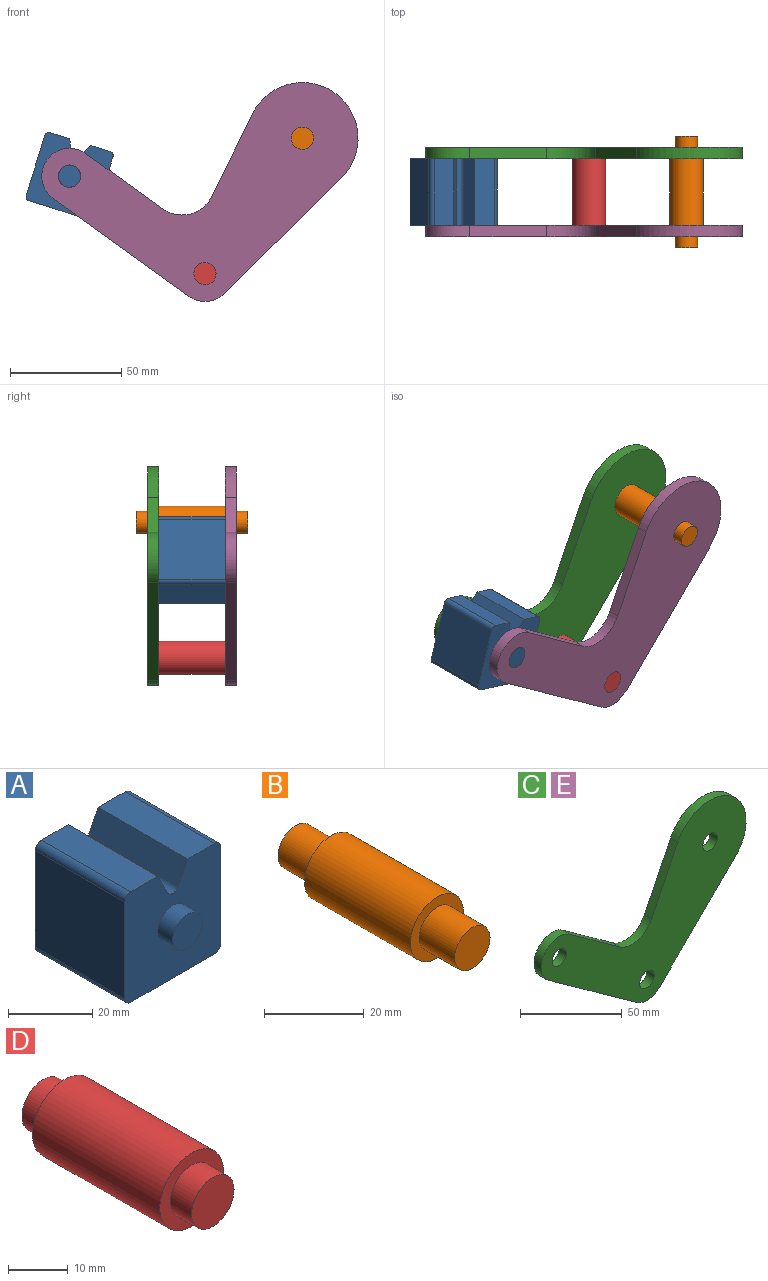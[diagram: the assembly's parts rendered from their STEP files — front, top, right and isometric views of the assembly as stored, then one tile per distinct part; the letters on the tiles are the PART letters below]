
ASSEMBLY  parts=5 mates=4
PART A: 18 faces, bbox 32.1x40x32.1 mm
  f0: plane 30x6.42mm, normal (0.89,0,0.45), area 215.4mm2, adj f4,f6,f10,f13
  f1: plane 30x6.42mm, normal (-0.89,0,0.45), area 215.4mm2, adj f2,f4,f10,f13
  f2: plane 30x9.04mm, normal (0,0,1), area 271.2mm2, adj f1,f4,f10,f14
  f3: plane 30x28.08mm, normal (1,0,0), area 842.3mm2, adj f4,f10,f14,f15
  f4: plane 32.08x32.08mm, normal (0,-1,0), area 900.6mm2, adj f0,f1,f2,f3,f5,f6,f7,f9
  f5: plane 30x28.08mm, normal (0,0,-1), area 842.3mm2, adj f4,f10,f15,f16
  f6: plane 30x9.04mm, normal (0,0,1), area 271.2mm2, adj f0,f4,f10,f17
  f7: plane 30x28.08mm, normal (-1,0,0), area 842.3mm2, adj f4,f10,f16,f17
  f8: plane 10x10mm, normal (0,-1,0), area 78.5mm2, adj f9
  f9: cylinder r=5mm len=10mm, axis (0,1,0), area 157.1mm2, adj f4,f8
  f10: plane 32.08x32.08mm, normal (0,1,0), area 900.6mm2, adj f0,f1,f2,f3,f5,f6,f7,f12
  f11: plane 10x10mm, normal (0,1,0), area 78.5mm2, adj f12
  f12: cylinder r=5mm len=10mm, axis (0,-1,0), area 157.1mm2, adj f10,f11
  f13: cylinder r=2mm len=30mm, axis (0,1,0), area 132.9mm2, adj f0,f1,f4,f10
  f14: cylinder r=2mm len=30mm, axis (0,1,0), area 94.2mm2, adj f2,f3,f4,f10
  f15: cylinder r=2mm len=30mm, axis (0,-1,0), area 94.2mm2, adj f3,f4,f5,f10
  f16: cylinder r=2mm len=30mm, axis (0,1,0), area 94.2mm2, adj f4,f5,f7,f10
  f17: cylinder r=2mm len=30mm, axis (0,-1,0), area 94.2mm2, adj f4,f6,f7,f10
PART B: 7 faces, bbox 15x50x15 mm
  f0: cylinder r=7.5mm len=30mm, axis (0,-1,0), area 1413.7mm2, adj f2,f5
  f1: cylinder r=5mm len=10mm, axis (0,1,0), area 314.2mm2, adj f2,f3
  f2: plane 15x15mm, normal (0,-1,0), area 98.2mm2, adj f0,f1
  f3: plane 10x10mm, normal (0,-1,0), area 78.5mm2, adj f1
  f4: cylinder r=5mm len=10mm, axis (0,-1,0), area 314.2mm2, adj f5,f6
  f5: plane 15x15mm, normal (0,1,0), area 98.2mm2, adj f0,f4
  f6: plane 10x10mm, normal (0,1,0), area 78.5mm2, adj f4
PART C: 13 faces, bbox 142.2x5x98.4 mm
  f0: plane 52.61x51.97mm, normal (0.7,0,-0.71), area 369.8mm2, adj f1,f9,f11,f12
  f1: cylinder r=25mm len=47.44mm, axis (0,-1,0), area 434.6mm2, adj f0,f2,f11,f12
  f2: plane 37.17x18.26mm, normal (-0.9,0,0.44), area 207.1mm2, adj f1,f3,f11,f12
  f3: cylinder r=15mm len=22.23mm, axis (0,-1,0), area 130.4mm2, adj f2,f4,f11,f12
  f4: plane 34.46x24.81mm, normal (0.58,0,0.81), area 212.3mm2, adj f3,f5,f11,f12
  f5: cylinder r=12.5mm len=22.64mm, axis (0,-1,0), area 196.3mm2, adj f4,f6,f11,f12
  f6: plane 60.86x43.82mm, normal (-0.58,0,-0.81), area 375mm2, adj f5,f9,f11,f12
  f7: cylinder r=5mm len=10mm, axis (0,-1,0), area 157.1mm2, adj f11,f12
  f8: cylinder r=5mm len=10mm, axis (0,-1,0), area 157.1mm2, adj f11,f12
  f9: cylinder r=12.5mm len=16.09mm, axis (0,-1,0), area 87.7mm2, adj f0,f6,f11,f12
  f10: cylinder r=5mm len=10mm, axis (0,-1,0), area 157.1mm2, adj f11,f12
  f11: plane 142.19x98.36mm, normal (0,1,0), area 5739.8mm2, adj f0,f1,f2,f3,f4,f5,f6,f7
  f12: plane 142.19x98.36mm, normal (0,-1,0), area 5739.8mm2, adj f0,f1,f2,f3,f4,f5,f6,f7
PART D: 7 faces, bbox 15x40x15 mm
  f0: cylinder r=7.5mm len=30mm, axis (0,-1,0), area 1413.7mm2, adj f2,f5
  f1: cylinder r=5mm len=10mm, axis (0,-1,0), area 157.1mm2, adj f2,f3
  f2: plane 15x15mm, normal (0,-1,0), area 98.2mm2, adj f0,f1
  f3: plane 10x10mm, normal (0,-1,0), area 78.5mm2, adj f1
  f4: cylinder r=5mm len=10mm, axis (0,1,0), area 157.1mm2, adj f5,f6
  f5: plane 15x15mm, normal (0,1,0), area 98.2mm2, adj f0,f4
  f6: plane 10x10mm, normal (0,1,0), area 78.5mm2, adj f4
PART E: same geometry as C
PLACE A rot(axis=(0,1,0),17.3deg) t=(0.32,-20,-31.96)mm
PLACE B t=(0,-20,0)mm fixed
PLACE C t=(0,15,0)mm
PLACE D t=(0,-20,0)mm
PLACE E t=(0,-20,0)mm
MATE fastened B.f0 <-> E.f1  axis (0,1,0) through (0,-15,0)mm
MATE revolute A.f9 <-> E.f5  axis (0,-1,0) through (-104.69,-15,-17.04)mm
MATE fastened C.f1 <-> B.f0  axis (0,-1,0) through (0,15,0)mm
MATE fastened D.f0 <-> E.f7  axis (0,-1,0) through (-43.82,-15,-60.86)mm
